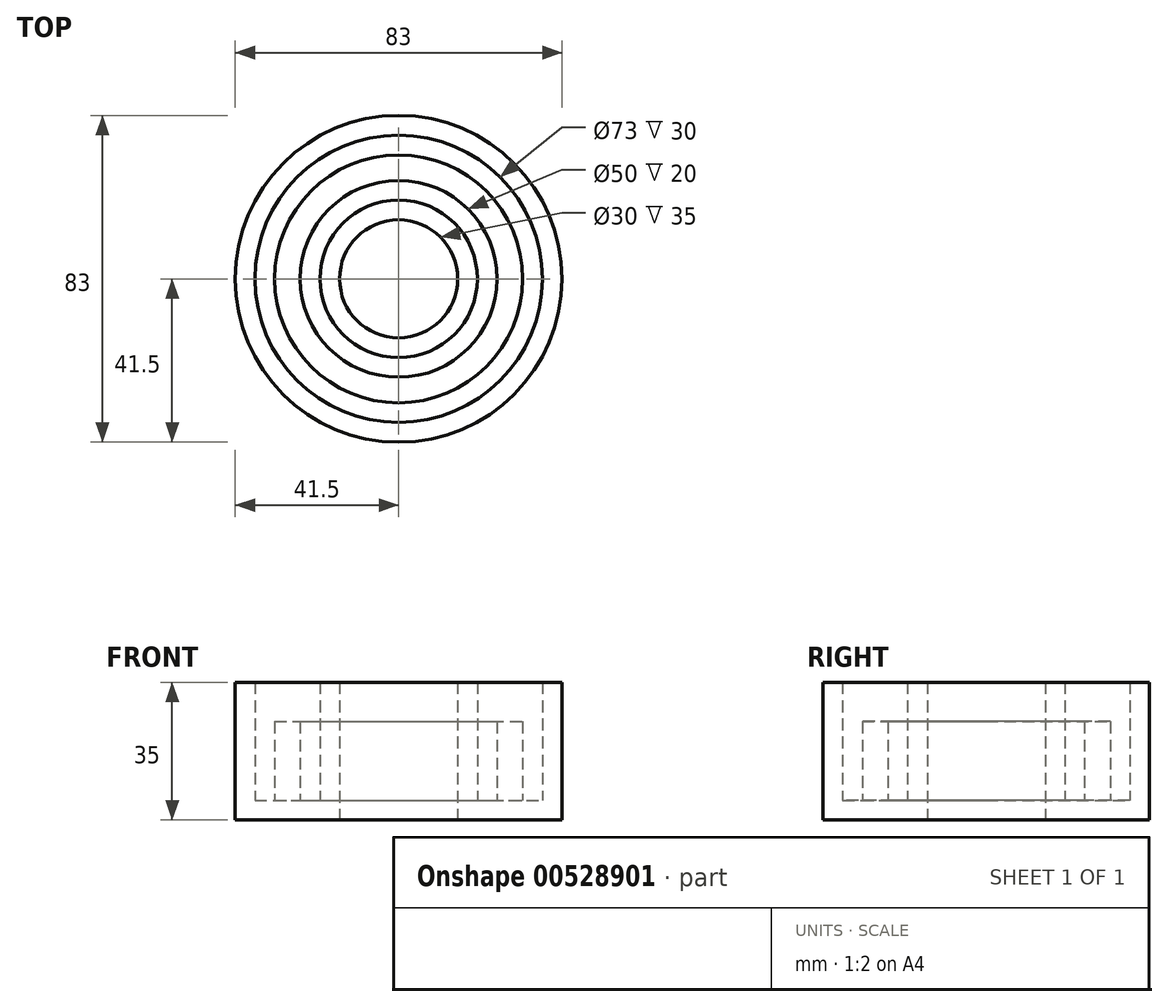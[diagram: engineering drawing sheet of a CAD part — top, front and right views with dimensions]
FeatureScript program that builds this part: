
annotation { "Feature Type Name" : "Feature", "Feature Type Description" : "" }
export const myFeature = defineFeature(function(context is Context, id is Id, definition is map)
    precondition{}
    {
        {
            var Q0;
            Q0=qCreatedBy(makeId("Front.planeOp"),FACE);
            var sketch = newSketch(context, id + "F0", { "sketchPlane" : qUnion([Q0])});
            skLineSegment(sketch, "E0", {"start": v(0, 0) * mm, "end": v(0, 33.34) * mm});
            skSolve(sketch);
        }
        {
            var Q0;
            Q0=qCreatedBy(makeId("Front.planeOp"),FACE);
            var sketch = newSketch(context, id + "F1", { "sketchPlane" : qUnion([Q0])});
            skLineSegment(sketch, "E1", {"start": v(41.5, 0) * mm, "end": v(41.5, 35) * mm});
            skLineSegment(sketch, "E2", {"start": v(41.5, 35) * mm, "end": v(36.5, 35) * mm});
            skLineSegment(sketch, "E3", {"start": v(36.5, 35) * mm, "end": v(36.5, 5) * mm});
            skLineSegment(sketch, "E4", {"start": v(36.5, 5) * mm, "end": v(31.5, 5) * mm});
            skLineSegment(sketch, "E5", {"start": v(31.5, 5) * mm, "end": v(31.5, 25) * mm});
            skLineSegment(sketch, "E6", {"start": v(31.5, 25) * mm, "end": v(25, 25) * mm});
            skLineSegment(sketch, "E7", {"start": v(25, 25) * mm, "end": v(25, 5) * mm});
            skLineSegment(sketch, "E8", {"start": v(41.5, 0) * mm, "end": v(15, 0) * mm});
            skLineSegment(sketch, "E9", {"start": v(15, 0) * mm, "end": v(15, 35) * mm});
            skLineSegment(sketch, "E10", {"start": v(15, 35) * mm, "end": v(20, 35) * mm});
            skLineSegment(sketch, "E11", {"start": v(20, 35) * mm, "end": v(20, 5) * mm});
            skLineSegment(sketch, "E12", {"start": v(20, 5) * mm, "end": v(25, 5) * mm});
            skSolve(sketch);
        }
        {
            var Q0;
            Q0 = qSketchRegion(id + "F1", true);
            var Q1;
            Q1=sQuery(id+"F0.wireOp",EDGE,"E0");
            revolve(context, id + "F2", {"entities" : qUnion([Q0]), "axis" : qUnion([Q1]), "revolveType" : RevolveType.FULL});
        }
    });
